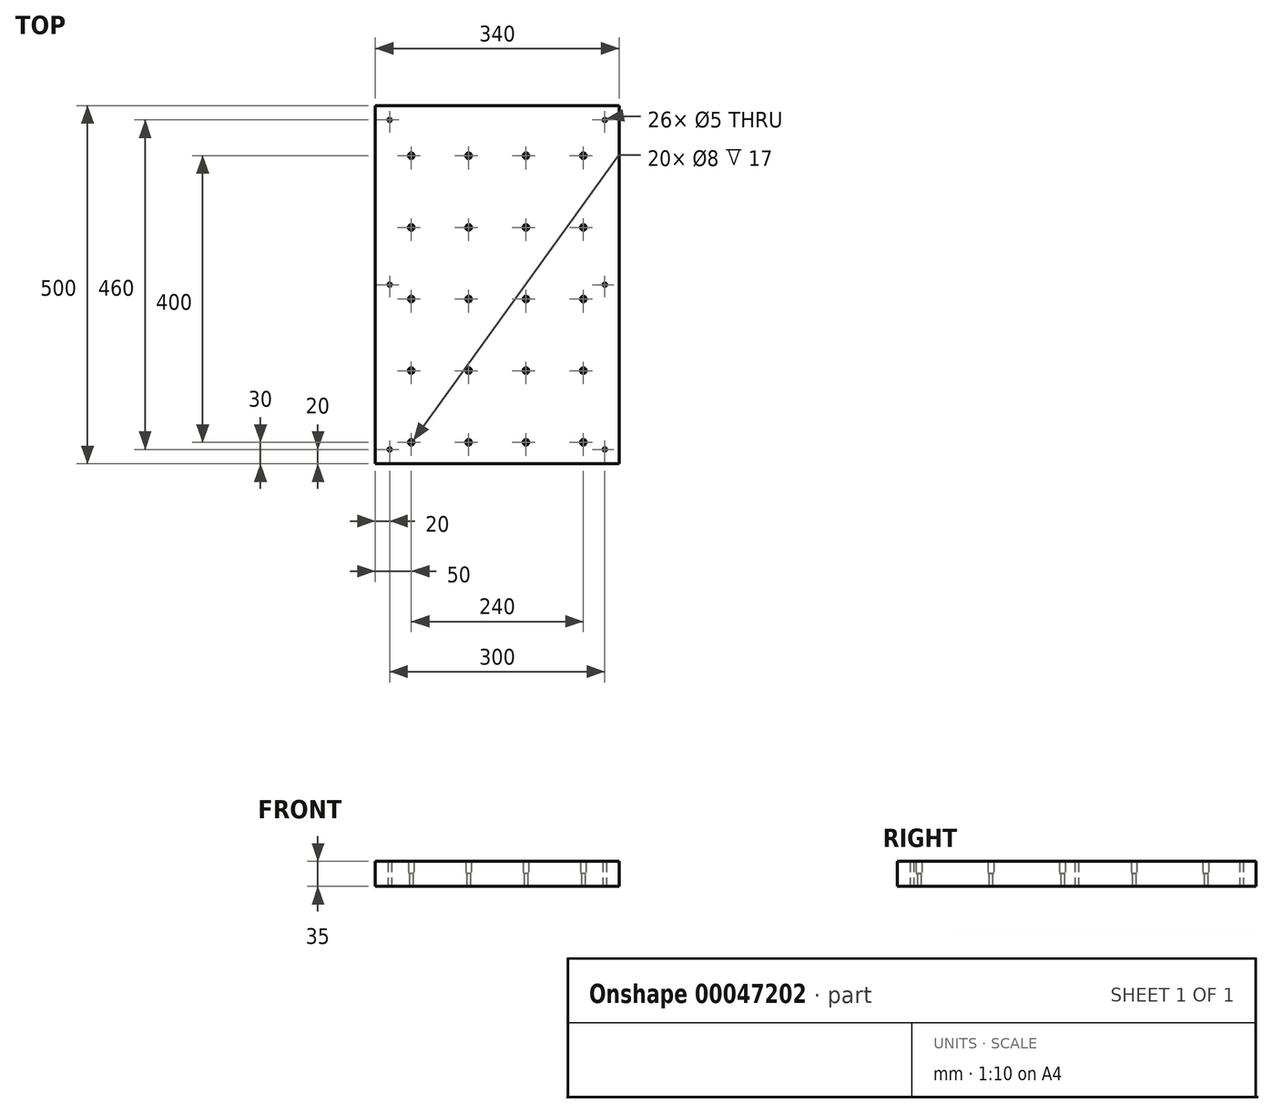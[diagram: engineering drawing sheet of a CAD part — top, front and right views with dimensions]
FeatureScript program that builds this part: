
annotation { "Feature Type Name" : "Feature", "Feature Type Description" : "" }
export const myFeature = defineFeature(function(context is Context, id is Id, definition is map)
    precondition{}
    {
        {
            var Q0;
            Q0=qCreatedBy(makeId("Top.planeOp"),FACE);
            var sketch = newSketch(context, id + "F0", { "sketchPlane" : qUnion([Q0])});
            skLineSegment(sketch, "E0.bottom", {"start": v(0, 0) * mm, "end": v(340, 0) * mm});
            skLineSegment(sketch, "E0.top", {"start": v(0, 500) * mm, "end": v(340, 500) * mm});
            skLineSegment(sketch, "E0.left", {"start": v(0, 0) * mm, "end": v(0, 500) * mm});
            skLineSegment(sketch, "E0.right", {"start": v(340, 0) * mm, "end": v(340, 500) * mm});
            skCircle(sketch, "E1", {"center": v(20, 480) * mm, "radius": 2.5 * mm});
            skLineSegment(sketch, "E2", {"start": v(170, 530.67) * mm, "end": v(170, -28.44) * mm, "construction": true});
            skCircle(sketch, "E3", {"center": v(20, 20) * mm, "radius": 2.5 * mm});
            skCircle(sketch, "E4.MirrorC", {"center": v(320, 480) * mm, "radius": 2.5 * mm});
            skCircle(sketch, "E5.MirrorC", {"center": v(320, 20) * mm, "radius": 2.5 * mm});
            skLineSegment(sketch, "E6", {"start": v(-116.5, 250) * mm, "end": v(426.25, 250) * mm, "construction": true});
            skCircle(sketch, "E7", {"center": v(20, 250) * mm, "radius": 2.5 * mm});
            skCircle(sketch, "E8.MirrorC", {"center": v(320, 250) * mm, "radius": 2.5 * mm});
            skCircle(sketch, "E9", {"center": v(50, 430) * mm, "radius": 4 * mm});
            skCircle(sketch, "E10", {"center": v(50, 430) * mm, "radius": 2.5 * mm});
            skCircle(sketch, "E11.0.1.0", {"center": v(50, 330) * mm, "radius": 4 * mm});
            skCircle(sketch, "E11.0.1.1", {"center": v(50, 330) * mm, "radius": 2.5 * mm});
            skCircle(sketch, "E11.0.2.0", {"center": v(50, 230) * mm, "radius": 4 * mm});
            skCircle(sketch, "E11.0.2.1", {"center": v(50, 230) * mm, "radius": 2.5 * mm});
            skCircle(sketch, "E11.0.3.0", {"center": v(50, 130) * mm, "radius": 4 * mm});
            skCircle(sketch, "E11.0.3.1", {"center": v(50, 130) * mm, "radius": 2.5 * mm});
            skCircle(sketch, "E11.0.4.0", {"center": v(50, 30) * mm, "radius": 4 * mm});
            skCircle(sketch, "E11.0.4.1", {"center": v(50, 30) * mm, "radius": 2.5 * mm});
            skCircle(sketch, "E11.1.0.0", {"center": v(130, 430) * mm, "radius": 4 * mm});
            skCircle(sketch, "E11.1.0.1", {"center": v(130, 430) * mm, "radius": 2.5 * mm});
            skCircle(sketch, "E11.1.1.0", {"center": v(130, 330) * mm, "radius": 4 * mm});
            skCircle(sketch, "E11.1.1.1", {"center": v(130, 330) * mm, "radius": 2.5 * mm});
            skCircle(sketch, "E11.1.2.0", {"center": v(130, 230) * mm, "radius": 4 * mm});
            skCircle(sketch, "E11.1.2.1", {"center": v(130, 230) * mm, "radius": 2.5 * mm});
            skCircle(sketch, "E11.1.3.0", {"center": v(130, 130) * mm, "radius": 4 * mm});
            skCircle(sketch, "E11.1.3.1", {"center": v(130, 130) * mm, "radius": 2.5 * mm});
            skCircle(sketch, "E11.1.4.0", {"center": v(130, 30) * mm, "radius": 4 * mm});
            skCircle(sketch, "E11.1.4.1", {"center": v(130, 30) * mm, "radius": 2.5 * mm});
            skCircle(sketch, "E11.2.0.0", {"center": v(210, 430) * mm, "radius": 4 * mm});
            skCircle(sketch, "E11.2.0.1", {"center": v(210, 430) * mm, "radius": 2.5 * mm});
            skCircle(sketch, "E11.2.1.0", {"center": v(210, 330) * mm, "radius": 4 * mm});
            skCircle(sketch, "E11.2.1.1", {"center": v(210, 330) * mm, "radius": 2.5 * mm});
            skCircle(sketch, "E11.2.2.0", {"center": v(210, 230) * mm, "radius": 4 * mm});
            skCircle(sketch, "E11.2.2.1", {"center": v(210, 230) * mm, "radius": 2.5 * mm});
            skCircle(sketch, "E11.2.3.0", {"center": v(210, 130) * mm, "radius": 4 * mm});
            skCircle(sketch, "E11.2.3.1", {"center": v(210, 130) * mm, "radius": 2.5 * mm});
            skCircle(sketch, "E11.2.4.0", {"center": v(210, 30) * mm, "radius": 4 * mm});
            skCircle(sketch, "E11.2.4.1", {"center": v(210, 30) * mm, "radius": 2.5 * mm});
            skCircle(sketch, "E11.3.0.0", {"center": v(290, 430) * mm, "radius": 4 * mm});
            skCircle(sketch, "E11.3.0.1", {"center": v(290, 430) * mm, "radius": 2.5 * mm});
            skCircle(sketch, "E11.3.1.0", {"center": v(290, 330) * mm, "radius": 4 * mm});
            skCircle(sketch, "E11.3.1.1", {"center": v(290, 330) * mm, "radius": 2.5 * mm});
            skCircle(sketch, "E11.3.2.0", {"center": v(290, 230) * mm, "radius": 4 * mm});
            skCircle(sketch, "E11.3.2.1", {"center": v(290, 230) * mm, "radius": 2.5 * mm});
            skCircle(sketch, "E11.3.3.0", {"center": v(290, 130) * mm, "radius": 4 * mm});
            skCircle(sketch, "E11.3.3.1", {"center": v(290, 130) * mm, "radius": 2.5 * mm});
            skCircle(sketch, "E11.3.4.0", {"center": v(290, 30) * mm, "radius": 4 * mm});
            skCircle(sketch, "E11.3.4.1", {"center": v(290, 30) * mm, "radius": 2.5 * mm});
            skLineSegment(sketch, "E11.direction1", {"start": v(50, 430) * mm, "end": v(130, 430) * mm, "construction": true});
            skLineSegment(sketch, "E11.direction2", {"start": v(50, 430) * mm, "end": v(50, 330) * mm, "construction": true});
            skSolve(sketch);
        }
        {
            var Q0;
            Q0=makeQuery(id+"F0.imprint","IMPRINT",FACE,{"disambiguationData":[TD([[makeQuery(id+"F0.imprint","IMPRINT",EDGE,{"derivedFrom":sQuery(id+"F0.wireOp",EDGE,"E0.bottom")}),1.0]])]});
            extrude(context, id + "F1", {"entities" : qUnion([Q0]), "depth" : 35 * mm});
        }
        {
            var Q0;
            Q0=makeQuery(id+"F0.imprint","IMPRINT",FACE,{"disambiguationData":[TD([[makeQuery(id+"F0.imprint","IMPRINT",EDGE,{"derivedFrom":sQuery(id+"F0.wireOp",EDGE,"E9")}),1.0]])]});
            var Q1;
            Q1=makeQuery(id+"F0.imprint","IMPRINT",FACE,{"disambiguationData":[TD([[makeQuery(id+"F0.imprint","IMPRINT",EDGE,{"derivedFrom":sQuery(id+"F0.wireOp",EDGE,"E11.1.0.0")}),1.0]])]});
            var Q2;
            Q2=makeQuery(id+"F0.imprint","IMPRINT",FACE,{"disambiguationData":[TD([[makeQuery(id+"F0.imprint","IMPRINT",EDGE,{"derivedFrom":sQuery(id+"F0.wireOp",EDGE,"E11.0.1.0")}),1.0]])]});
            var Q3;
            Q3=makeQuery(id+"F0.imprint","IMPRINT",FACE,{"disambiguationData":[TD([[makeQuery(id+"F0.imprint","IMPRINT",EDGE,{"derivedFrom":sQuery(id+"F0.wireOp",EDGE,"E11.1.1.0")}),1.0]])]});
            var Q4;
            Q4=makeQuery(id+"F0.imprint","IMPRINT",FACE,{"disambiguationData":[TD([[makeQuery(id+"F0.imprint","IMPRINT",EDGE,{"derivedFrom":sQuery(id+"F0.wireOp",EDGE,"E11.2.0.0")}),1.0]])]});
            var Q5;
            Q5=makeQuery(id+"F0.imprint","IMPRINT",FACE,{"disambiguationData":[TD([[makeQuery(id+"F0.imprint","IMPRINT",EDGE,{"derivedFrom":sQuery(id+"F0.wireOp",EDGE,"E11.2.1.0")}),1.0]])]});
            var Q6;
            Q6=makeQuery(id+"F0.imprint","IMPRINT",FACE,{"disambiguationData":[TD([[makeQuery(id+"F0.imprint","IMPRINT",EDGE,{"derivedFrom":sQuery(id+"F0.wireOp",EDGE,"E11.3.1.0")}),1.0]])]});
            var Q7;
            Q7=makeQuery(id+"F0.imprint","IMPRINT",FACE,{"disambiguationData":[TD([[makeQuery(id+"F0.imprint","IMPRINT",EDGE,{"derivedFrom":sQuery(id+"F0.wireOp",EDGE,"E11.3.0.0")}),1.0]])]});
            var Q8;
            Q8=makeQuery(id+"F0.imprint","IMPRINT",FACE,{"disambiguationData":[TD([[makeQuery(id+"F0.imprint","IMPRINT",EDGE,{"derivedFrom":sQuery(id+"F0.wireOp",EDGE,"E11.0.2.0")}),1.0]])]});
            var Q9;
            Q9=makeQuery(id+"F0.imprint","IMPRINT",FACE,{"disambiguationData":[TD([[makeQuery(id+"F0.imprint","IMPRINT",EDGE,{"derivedFrom":sQuery(id+"F0.wireOp",EDGE,"E11.1.2.0")}),1.0]])]});
            var Q10;
            Q10=makeQuery(id+"F0.imprint","IMPRINT",FACE,{"disambiguationData":[TD([[makeQuery(id+"F0.imprint","IMPRINT",EDGE,{"derivedFrom":sQuery(id+"F0.wireOp",EDGE,"E11.2.2.0")}),1.0]])]});
            var Q11;
            Q11=makeQuery(id+"F0.imprint","IMPRINT",FACE,{"disambiguationData":[TD([[makeQuery(id+"F0.imprint","IMPRINT",EDGE,{"derivedFrom":sQuery(id+"F0.wireOp",EDGE,"E11.3.2.0")}),1.0]])]});
            var Q12;
            Q12=makeQuery(id+"F0.imprint","IMPRINT",FACE,{"disambiguationData":[TD([[makeQuery(id+"F0.imprint","IMPRINT",EDGE,{"derivedFrom":sQuery(id+"F0.wireOp",EDGE,"E11.0.3.0")}),1.0]])]});
            var Q13;
            Q13=makeQuery(id+"F0.imprint","IMPRINT",FACE,{"disambiguationData":[TD([[makeQuery(id+"F0.imprint","IMPRINT",EDGE,{"derivedFrom":sQuery(id+"F0.wireOp",EDGE,"E11.1.3.0")}),1.0]])]});
            var Q14;
            Q14=makeQuery(id+"F0.imprint","IMPRINT",FACE,{"disambiguationData":[TD([[makeQuery(id+"F0.imprint","IMPRINT",EDGE,{"derivedFrom":sQuery(id+"F0.wireOp",EDGE,"E11.2.3.0")}),1.0]])]});
            var Q15;
            Q15=makeQuery(id+"F0.imprint","IMPRINT",FACE,{"disambiguationData":[TD([[makeQuery(id+"F0.imprint","IMPRINT",EDGE,{"derivedFrom":sQuery(id+"F0.wireOp",EDGE,"E11.3.3.0")}),1.0]])]});
            var Q16;
            Q16=makeQuery(id+"F0.imprint","IMPRINT",FACE,{"disambiguationData":[TD([[makeQuery(id+"F0.imprint","IMPRINT",EDGE,{"derivedFrom":sQuery(id+"F0.wireOp",EDGE,"E11.0.4.0")}),1.0]])]});
            var Q17;
            Q17=makeQuery(id+"F0.imprint","IMPRINT",FACE,{"disambiguationData":[TD([[makeQuery(id+"F0.imprint","IMPRINT",EDGE,{"derivedFrom":sQuery(id+"F0.wireOp",EDGE,"E11.1.4.0")}),1.0]])]});
            var Q18;
            Q18=makeQuery(id+"F0.imprint","IMPRINT",FACE,{"disambiguationData":[TD([[makeQuery(id+"F0.imprint","IMPRINT",EDGE,{"derivedFrom":sQuery(id+"F0.wireOp",EDGE,"E11.2.4.0")}),1.0]])]});
            var Q19;
            Q19=makeQuery(id+"F0.imprint","IMPRINT",FACE,{"disambiguationData":[TD([[makeQuery(id+"F0.imprint","IMPRINT",EDGE,{"derivedFrom":sQuery(id+"F0.wireOp",EDGE,"E11.3.4.0")}),1.0]])]});
            extrude(context, id + "F2", {"entities" : qUnion([Q0, Q1, Q2, Q3, Q4, Q5, Q6, Q7, Q8, Q9, Q10, Q11, Q12, Q13, Q14, Q15, Q16, Q17, Q18, Q19]), "operationType" : NewBodyOperationType.ADD, "depth" : 18 * mm});
        }
    });
